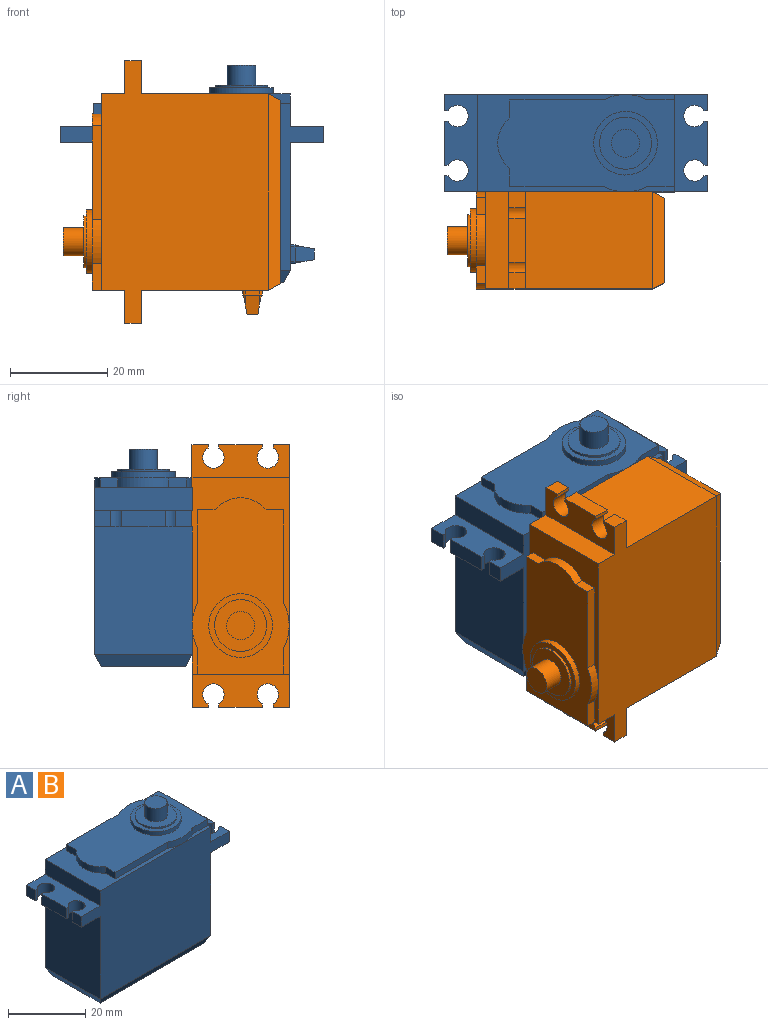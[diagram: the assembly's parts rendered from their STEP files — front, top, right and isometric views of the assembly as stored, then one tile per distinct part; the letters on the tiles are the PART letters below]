
ASSEMBLY  parts=2 mates=1
PART A: 70 faces, bbox 54.1x20x44.7 mm
  f0: plane 10x1.1mm, normal (0,0,1), area 7.6mm2, adj f13,f16,f60,f61
  f1: plane 30.4x20mm, normal (0,0,1), area 159.3mm2, adj f12,f15,f16,f54,f55,f56,f57,f58
  f2: plane 4x3mm, normal (0.17,-0.98,0), area 11.3mm2, adj f3,f4,f8,f9,f10,f49
  f3: cone r=0.5mm half-angle=10deg, axis (-1,0,0), area 0.5mm2, adj f2,f4,f49
  f4: plane 6x4mm, normal (0.17,0,-0.98), area 23.5mm2, adj f2,f3,f5,f6,f10,f49
  f5: cone r=0.5mm half-angle=10deg, axis (-1,0,0), area 0.5mm2, adj f4,f6,f49
  f6: plane 4x3mm, normal (0.17,0.98,0), area 11.3mm2, adj f4,f5,f7,f8,f10,f49
  f7: cone r=0.5mm half-angle=10deg, axis (-1,0,0), area 0.5mm2, adj f6,f8,f49
  f8: plane 6x4mm, normal (0.17,0,0.98), area 23.5mm2, adj f2,f6,f7,f9,f10,f49
  f9: cone r=0.5mm half-angle=10deg, axis (-1,0,0), area 0.5mm2, adj f2,f8,f49
  f10: plane 5.24x2.24mm, normal (1,0,0), area 11.7mm2, adj f2,f4,f6,f8
  f11: plane 26.2x20mm, normal (1,0,0), area 496.2mm2, adj f15,f16,f22,f23,f45,f46,f47,f48
  f12: plane 20x4.75mm, normal (-1,0,0), area 95mm2, adj f1,f15,f16,f35
  f13: plane 20x6.75mm, normal (1,0,0), area 130.6mm2, adj f0,f15,f16,f17,f24,f59,f60,f63
  f14: plane 26.2x20mm, normal (-1,0,0), area 524mm2, adj f15,f16,f19,f34
  f15: plane 54.1x34.3mm, normal (0,-1,0), area 1431.6mm2, adj f1,f11,f12,f13,f14,f17,f21,f23
  f16: plane 54.1x34.3mm, normal (0,1,0), area 1431.6mm2, adj f0,f1,f11,f12,f13,f14,f20,f23
  f17: plane 10x1.1mm, normal (0,0,1), area 7.6mm2, adj f13,f15,f58,f59
  f18: plane 37.8x17.4mm, normal (0,0,-1), area 657.7mm2, adj f19,f20,f21,f22
  f19: plane 20x2.5mm, normal (-0.89,0,-0.46), area 52.7mm2, adj f14,f18,f20,f21
  f20: plane 40.4x2.5mm, normal (0,0.89,-0.46), area 110.2mm2, adj f16,f18,f19,f22
  f21: plane 40.4x2.5mm, normal (0,-0.89,-0.46), area 110.2mm2, adj f15,f18,f19,f22
  f22: plane 20x2.5mm, normal (0.89,0,-0.46), area 52.7mm2, adj f11,f18,f20,f21
  f23: plane 20x6.85mm, normal (0,0,-1), area 104.2mm2, adj f11,f15,f16,f25,f26,f27,f28,f29
  f24: plane 20x6.85mm, normal (0,0,1), area 104.2mm2, adj f13,f15,f16,f25,f26,f27,f28,f29
  f25: plane 9x3.35mm, normal (1,0,0), area 30.2mm2, adj f23,f24,f30,f33
  f26: plane 3.35x3.3mm, normal (1,0,0), area 11.1mm2, adj f16,f23,f24,f29
  f27: plane 3.35x3.3mm, normal (1,0,0), area 11.1mm2, adj f15,f23,f24,f32
  f28: cylinder r=2.2mm len=4.4mm, axis (0,0,1), area 38.6mm2, adj f23,f24,f29,f30
  f29: plane 3.35x0.74mm, normal (0,-1,0), area 2.5mm2, adj f23,f24,f26,f28
  f30: plane 3.35x0.74mm, normal (0,1,0), area 2.5mm2, adj f23,f24,f25,f28
  f31: cylinder r=2.2mm len=4.4mm, axis (0,0,1), area 38.6mm2, adj f23,f24,f32,f33
  f32: plane 3.35x0.74mm, normal (0,1,0), area 2.5mm2, adj f23,f24,f27,f31
  f33: plane 3.35x0.74mm, normal (0,-1,0), area 2.5mm2, adj f23,f24,f25,f31
  f34: plane 20x6.85mm, normal (0,0,-1), area 104.2mm2, adj f14,f15,f16,f36,f37,f38,f39,f40
  f35: plane 20x6.85mm, normal (0,0,1), area 104.2mm2, adj f12,f15,f16,f36,f37,f38,f39,f40
  f36: plane 9x3.35mm, normal (-1,0,0), area 30.2mm2, adj f34,f35,f41,f44
  f37: plane 3.35x3.3mm, normal (-1,0,0), area 11.1mm2, adj f16,f34,f35,f40
  f38: plane 3.35x3.3mm, normal (-1,0,0), area 11.1mm2, adj f15,f34,f35,f43
  f39: cylinder r=2.2mm len=4.4mm, axis (0,0,1), area 38.6mm2, adj f34,f35,f40,f41
  f40: plane 3.35x0.74mm, normal (0,-1,0), area 2.5mm2, adj f34,f35,f37,f39
  f41: plane 3.35x0.74mm, normal (0,1,0), area 2.5mm2, adj f34,f35,f36,f39
  f42: cylinder r=2.2mm len=4.4mm, axis (0,0,1), area 38.6mm2, adj f34,f35,f43,f44
  f43: plane 3.35x0.74mm, normal (0,1,0), area 2.5mm2, adj f34,f35,f38,f42
  f44: plane 3.35x0.74mm, normal (0,-1,0), area 2.5mm2, adj f34,f35,f36,f42
  f45: plane 3x1mm, normal (0,-1,0), area 3mm2, adj f11,f49,f50,f53
  f46: plane 6x1mm, normal (0,0,-1), area 6mm2, adj f11,f49,f50,f51
  f47: plane 3x1mm, normal (0,1,0), area 3mm2, adj f11,f49,f51,f52
  f48: plane 6x1mm, normal (0,0,1), area 6mm2, adj f11,f49,f52,f53
  f49: plane 7x4mm, normal (1,0,0), area 3.6mm2, adj f2,f3,f4,f5,f6,f7,f8,f9
  f50: cylinder r=0.5mm len=1mm, axis (-1,0,0), area 0.8mm2, adj f11,f45,f46,f49
  f51: cylinder r=0.5mm len=1mm, axis (1,0,0), area 0.8mm2, adj f11,f46,f47,f49
  f52: cylinder r=0.5mm len=1mm, axis (-1,0,0), area 0.8mm2, adj f11,f47,f48,f49
  f53: cylinder r=0.5mm len=1mm, axis (1,0,0), area 0.8mm2, adj f11,f45,f48,f49
  f54: plane 3.65x2mm, normal (-1,0,0), area 7.3mm2, adj f1,f55,f62,f63
  f55: cylinder r=6.76mm len=10.5mm, axis (0,0,-1), area 24mm2, adj f1,f54,f56,f63
  f56: plane 3.65x2mm, normal (-1,0,0), area 7.3mm2, adj f1,f55,f57,f63
  f57: plane 19.24x2mm, normal (0,-1,0), area 38.5mm2, adj f1,f56,f58,f63
  f58: cylinder r=10mm len=9.12mm, axis (0,0,-1), area 18.9mm2, adj f1,f17,f57,f59,f63
  f59: plane 5.44x2mm, normal (0,-1,0), area 10.9mm2, adj f13,f17,f58,f63
  f60: plane 5.44x2mm, normal (0,1,0), area 10.9mm2, adj f0,f13,f61,f63
  f61: cylinder r=10mm len=9.12mm, axis (0,0,-1), area 18.9mm2, adj f0,f1,f60,f62,f63
  f62: plane 19.24x2mm, normal (0,1,0), area 38.5mm2, adj f1,f54,f61,f63
  f63: plane 36.3x20mm, normal (0,0,1), area 498.7mm2, adj f13,f54,f55,f56,f57,f58,f59,f60
  f64: cylinder r=6.55mm len=13.1mm, axis (0,0,-1), area 51.4mm2, adj f63,f65
  f65: plane 13.1x13.1mm, normal (0,0,1), area 44.9mm2, adj f64,f66
  f66: cylinder r=5.35mm len=10.7mm, axis (0,0,-1), area 16.8mm2, adj f65,f67
  f67: plane 10.7x10.7mm, normal (0,0,1), area 63.5mm2, adj f66,f68
  f68: cylinder r=2.9mm len=5.8mm, axis (0,0,-1), area 75.6mm2, adj f67,f69
  f69: plane 5.8x5.8mm, normal (0,0,1), area 26.4mm2, adj f68
PART B: same geometry as A
PLACE A t=(8.64,-25.31,1.74)mm
PLACE B rot(axis=(0.71,0,-0.71),180deg) t=(26.88,-45.31,20.35)mm
MATE planar A.f15 <-> B.f15  axis (0,-1,0) through (8.64,-35.31,21.73)mm
